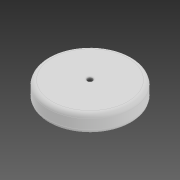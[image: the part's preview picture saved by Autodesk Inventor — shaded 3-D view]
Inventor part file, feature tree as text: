
AUTODESK INVENTOR PART (.ipt)
format: ipt  version: 2020 (Build 240168000, 168)  size: 110,080 bytes
history: native  units: in
note: dims shown in document units (in); Inventor stores cm internally (conversion verified against a paired STEP export)
features: extrude x1, fillet x1, sketch x1
ambient origin geometry x8: Origin, YZ Plane, XZ Plane, XY Plane, X Axis, Y Axis, Z Axis, Center Point
bodies: Solid1 (feature_tree)
feature tree (3):
  extrude  "Extrusion1"  Depth=0.1575in
  fillet  "Fillet1"  Radius=0.6693in
  sketch  "Sketch1"  dims[d0=3.1496in d1=0.1969in d2=0.6693in d3=0.0in d4=0.1575in]
